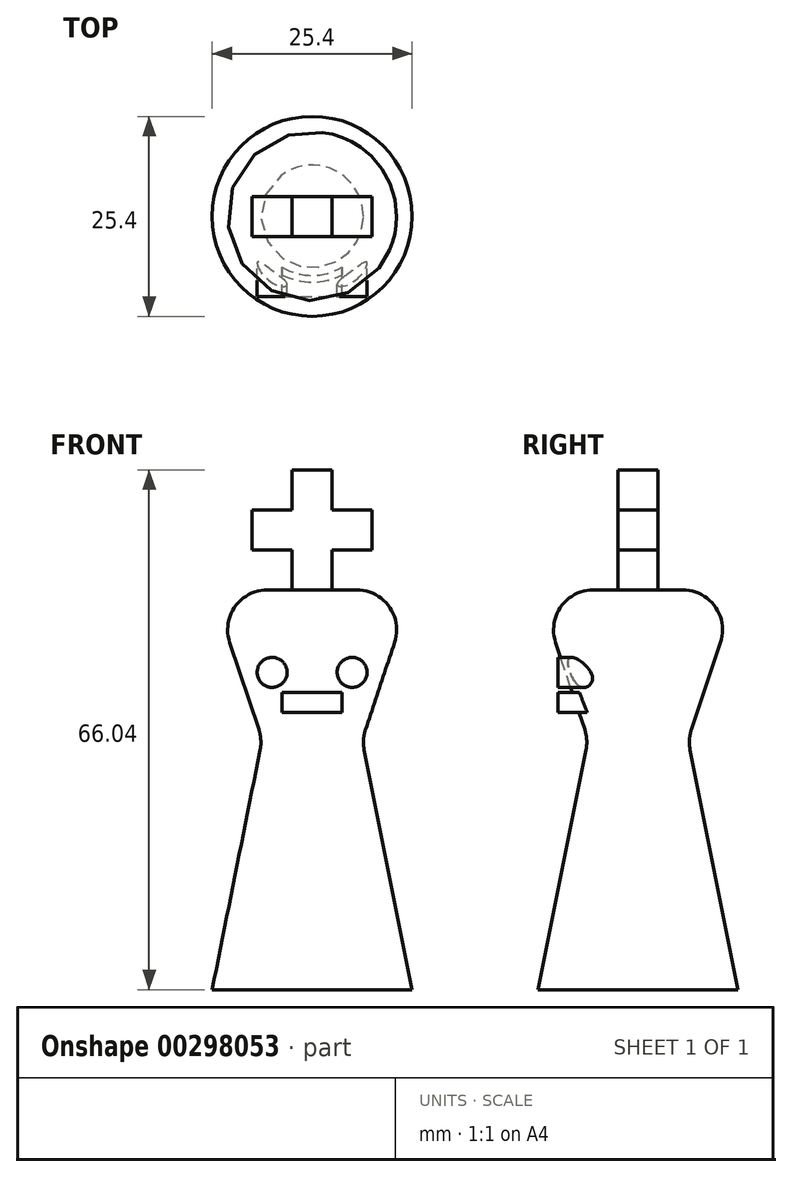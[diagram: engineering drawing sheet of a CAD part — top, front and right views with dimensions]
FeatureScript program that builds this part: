
annotation { "Feature Type Name" : "Feature", "Feature Type Description" : "" }
export const myFeature = defineFeature(function(context is Context, id is Id, definition is map)
    precondition{}
    {
        {
            var Q0;
            Q0=qCreatedBy(makeId("Front.planeOp"),FACE);
            var sketch = newSketch(context, id + "F0", { "sketchPlane" : qUnion([Q0])});
            skLineSegment(sketch, "E0", {"start": v(0, 0) * mm, "end": v(25.4, 0) * mm});
            skLineSegment(sketch, "E1", {"start": v(25.4, 0) * mm, "end": v(19.05, 31.75) * mm});
            skLineSegment(sketch, "E2", {"start": v(19.05, 31.75) * mm, "end": v(25.4, 50.8) * mm});
            skLineSegment(sketch, "E3", {"start": v(25.4, 50.8) * mm, "end": v(0, 50.8) * mm});
            skLineSegment(sketch, "E4", {"start": v(0, 50.8) * mm, "end": v(6.35, 31.75) * mm});
            skLineSegment(sketch, "E5", {"start": v(6.35, 31.75) * mm, "end": v(0, 0) * mm});
            skLineSegment(sketch, "E6", {"start": v(6.35, 31.75) * mm, "end": v(19.05, 31.75) * mm, "construction": true});
            skLineSegment(sketch, "E7", {"start": v(12.7, 50.8) * mm, "end": v(12.7, 0) * mm});
            skPoint(sketch, "E8", {"position": v(12.7, 31.75) * mm});
            skSolve(sketch);
        }
        {
            var Q0;
            {var subQ1=sQuery(id+"F0.wireOp",EDGE,"E4");Q0=makeQuery(id+"F0.imprint","IMPRINT",FACE,{"disambiguationData":[TD([[makeQuery(id+"F0.imprint","IMPRINT",EDGE,{"derivedFrom":subQ1}),1.0]])]});}
            var Q1;
            Q1=sQuery(id+"F0.wireOp",EDGE,"E7");
            revolve(context, id + "F1", {"entities" : qUnion([Q0]), "axis" : qUnion([Q1]), "revolveType" : RevolveType.FULL});
        }
        {
            var Q0;
            Q0=makeQuery(id+"F1.opRevolve","SWEPT_EDGE",EDGE,{"disambiguationData":[OSD([sQuery(id+"F0.wireOp",EDGE,"E4"),sQuery(id+"F0.wireOp",EDGE,"E5")])]});
            var Q1;
            Q1=makeQuery(id+"F1.opRevolve","SWEPT_EDGE",EDGE,{"disambiguationData":[OSD([sQuery(id+"F0.wireOp",EDGE,"E3"),sQuery(id+"F0.wireOp",EDGE,"E4")])]});
            fillet(context, id + "F2", {"entities" : qUnion([Q0, Q1]), "radius" : 5.08 * mm, "tangentPropagation" : true, "allowEdgeOverflow" : false});
        }
        {
            var Q0;
            Q0=qCreatedBy(makeId("Front.planeOp"),FACE);
            var sketch = newSketch(context, id + "F3", { "sketchPlane" : qUnion([Q0])});
            skLineSegment(sketch, "E9", {"start": v(10.16, 50.8) * mm, "end": v(10.16, 55.88) * mm});
            skLineSegment(sketch, "E10", {"start": v(10.16, 55.88) * mm, "end": v(5.08, 55.88) * mm});
            skLineSegment(sketch, "E11", {"start": v(5.08, 55.88) * mm, "end": v(5.08, 60.96) * mm});
            skLineSegment(sketch, "E12", {"start": v(5.08, 60.96) * mm, "end": v(10.16, 60.96) * mm});
            skLineSegment(sketch, "E13", {"start": v(10.16, 60.96) * mm, "end": v(10.16, 66.04) * mm});
            skLineSegment(sketch, "E14", {"start": v(10.16, 66.04) * mm, "end": v(15.24, 66.04) * mm});
            skLineSegment(sketch, "E15", {"start": v(15.24, 66.04) * mm, "end": v(15.24, 60.96) * mm});
            skLineSegment(sketch, "E16", {"start": v(15.24, 60.96) * mm, "end": v(20.32, 60.96) * mm});
            skLineSegment(sketch, "E17", {"start": v(20.32, 60.96) * mm, "end": v(20.32, 55.88) * mm});
            skLineSegment(sketch, "E18", {"start": v(20.32, 55.88) * mm, "end": v(15.24, 55.88) * mm});
            skLineSegment(sketch, "E19", {"start": v(15.24, 50.8) * mm, "end": v(10.16, 50.8) * mm});
            skLineSegment(sketch, "E20", {"start": v(15.24, 55.88) * mm, "end": v(15.24, 50.8) * mm});
            skPoint(sketch, "E21", {"position": v(12.7, 50.8) * mm});
            skSolve(sketch);
        }
        {
            var Q0;
            Q0=makeQuery(id+"F3.imprint","IMPRINT",FACE,{"disambiguationData":[TD([[makeQuery(id+"F3.imprint","IMPRINT",EDGE,{"derivedFrom":sQuery(id+"F3.wireOp",EDGE,"E9")}),-1.0]])]});
            extrude(context, id + "F4", {"entities" : qUnion([Q0]), "operationType" : NewBodyOperationType.ADD, "endBound" : BoundingType.SYMMETRIC, "depth" : 5.08 * mm});
        }
        {
            var Q0;
            Q0=qCreatedBy(makeId("Front.planeOp"),FACE);
            var sketch = newSketch(context, id + "F5", { "sketchPlane" : qUnion([Q0])});
            skCircle(sketch, "E22", {"center": v(7.62, 40.3) * mm, "radius": 1.9 * mm});
            skCircle(sketch, "E23", {"center": v(17.78, 40.3) * mm, "radius": 1.9 * mm});
            skLineSegment(sketch, "E24.bottom", {"start": v(8.9, 37.76) * mm, "end": v(16.52, 37.76) * mm});
            skLineSegment(sketch, "E24.top", {"start": v(8.9, 35.22) * mm, "end": v(16.52, 35.22) * mm});
            skLineSegment(sketch, "E24.left", {"start": v(8.9, 37.76) * mm, "end": v(8.9, 35.22) * mm});
            skLineSegment(sketch, "E24.right", {"start": v(16.52, 37.76) * mm, "end": v(16.52, 35.22) * mm});
            skLineSegment(sketch, "E25", {"start": v(7.62, 40.3) * mm, "end": v(17.78, 40.3) * mm, "construction": true});
            skLineSegment(sketch, "E26", {"start": v(12.7, 40.3) * mm, "end": v(12.7, 44.11) * mm, "construction": true});
            skSolve(sketch);
        }
        {
            var Q0;
            Q0 = qSketchRegion(id + "F5", true);
            extrude(context, id + "F6", {"entities" : qUnion([Q0]), "operationType" : NewBodyOperationType.ADD, "depth" : 10.16 * mm});
        }
    });
